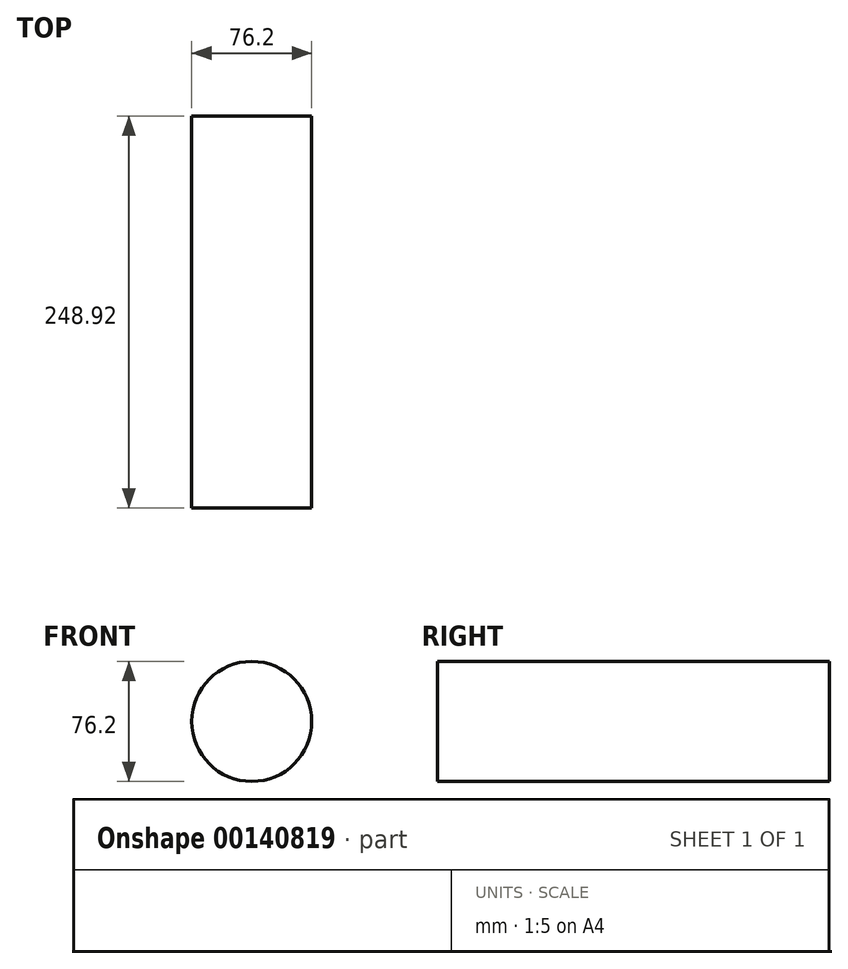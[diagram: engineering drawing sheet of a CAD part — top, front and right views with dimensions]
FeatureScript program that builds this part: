
annotation { "Feature Type Name" : "Feature", "Feature Type Description" : "" }
export const myFeature = defineFeature(function(context is Context, id is Id, definition is map)
    precondition{}
    {
        {
            var Q0;
            Q0=qCreatedBy(makeId("Front.planeOp"),FACE);
            var sketch = newSketch(context, id + "F0", { "sketchPlane" : qUnion([Q0])});
            skCircle(sketch, "E0", {"center": v(0, 0) * mm, "radius": 38.1 * mm});
            skSolve(sketch);
        }
        {
            var Q0;
            Q0=makeQuery(id+"F0.imprint","IMPRINT",FACE,{"disambiguationData":[TD([[makeQuery(id+"F0.imprint","IMPRINT",EDGE,{"derivedFrom":sQuery(id+"F0.wireOp",EDGE,"E0")}),1.0]])]});
            extrude(context, id + "F1", {"entities" : qUnion([Q0]), "endBound" : BoundingType.SYMMETRIC, "depth" : 248.92 * mm});
        }
    });
